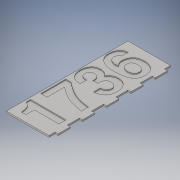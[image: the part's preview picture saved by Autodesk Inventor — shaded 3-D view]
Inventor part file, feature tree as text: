
AUTODESK INVENTOR PART (.ipt)
format: ipt  version: 2016 (Build 200138000, 138)  size: 237,568 bytes
history: native  units: in
note: dims shown in document units (in); Inventor stores cm internally (conversion verified against a paired STEP export)
features: extrude x3, sketch x3
ambient origin geometry x8: Origin, YZ Plane, XZ Plane, XY Plane, X Axis, Y Axis, Z Axis, Center Point
bodies: Solid1 (feature_tree)
feature tree (6):
  extrude  "Extrusion1"  Depth=10.0in
  extrude  "Extrusion2"  Depth=1.9685in
  sketch  "Sketch1"  dims[d0=3.5in d1=10.0in]
  sketch  "Sketch3"  dims[d2=0.125in d3=0.0in d4=1.9685in d6=2.0in d7=0.3937in d9=1.0in]
  sketch  "Sketch4"  dims[d11=0.125in d12=0.0in d14=0.0in d15=0.075in]
  extrude  "Extrusion3"  Depth=0.075in TaperAngle=0.0deg
